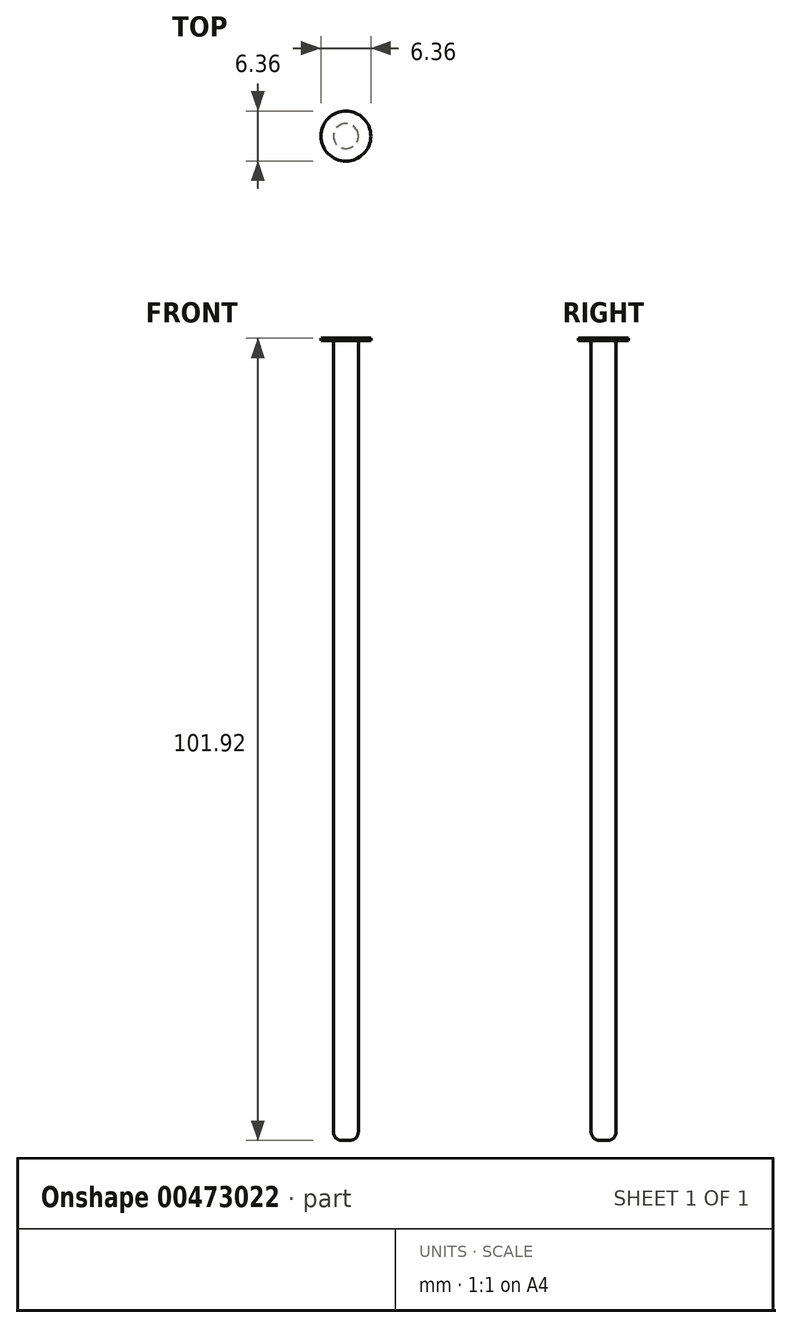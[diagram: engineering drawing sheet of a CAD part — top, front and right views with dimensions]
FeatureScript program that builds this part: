
annotation { "Feature Type Name" : "Feature", "Feature Type Description" : "" }
export const myFeature = defineFeature(function(context is Context, id is Id, definition is map)
    precondition{}
    {
        {
            var Q0;
            Q0=qCreatedBy(makeId("Top.planeOp"),FACE);
            var sketch = newSketch(context, id + "F0", { "sketchPlane" : qUnion([Q0])});
            skCircle(sketch, "E0", {"center": v(0, 0) * mm, "radius": 1.59 * mm});
            skSolve(sketch);
        }
        {
            var Q0;
            Q0=makeQuery(id+"F0.imprint","IMPRINT",FACE,{"disambiguationData":[TD([[makeQuery(id+"F0.imprint","IMPRINT",EDGE,{"derivedFrom":sQuery(id+"F0.wireOp",EDGE,"E0")}),1.0]])]});
            extrude(context, id + "F1", {"entities" : qUnion([Q0]), "depth" : 101.6 * mm});
        }
        {
            var Q0;
            Q0=makeQuery(id+"F1.opExtrude","CAP_FACE",FACE,{"disambiguationData":[OSD([sQuery(id+"F0.wireOp",EDGE,"E0")])],"isStart":false});
            var sketch = newSketch(context, id + "F2", { "sketchPlane" : qUnion([Q0])});
            skCircle(sketch, "E1", {"center": v(0, 0) * mm, "radius": 3.18 * mm});
            skSolve(sketch);
        }
        {
            var Q0;
            Q0=makeQuery(id+"F2.imprint","IMPRINT",FACE,{"disambiguationData":[TD([[makeQuery(id+"F2.imprint","IMPRINT",EDGE,{"derivedFrom":sQuery(id+"F2.wireOp",EDGE,"E1")}),1.0]])]});
            var Q1;
            Q1=makeQuery(id+"F2.imprint","IMPRINT",FACE,{"disambiguationData":[TD([[makeQuery(id+"F2.imprint","IMPRINT",EDGE,{"derivedFrom":makeQuery(id+"F1.opExtrude","CAP_EDGE",EDGE,{"disambiguationData":[OSD([sQuery(id+"F0.wireOp",EDGE,"E0")])],"isStart":false})}),1.0]])]});
            extrude(context, id + "F3", {"entities" : qUnion([Q0, Q1]), "operationType" : NewBodyOperationType.ADD, "depth" : 0.32 * mm});
        }
        {
            var Q0;
            Q0=makeQuery(id+"F1.opExtrude","CAP_EDGE",EDGE,{"disambiguationData":[OSD([sQuery(id+"F0.wireOp",EDGE,"E0")])],"isStart":true});
            fillet(context, id + "F4", {"entities" : qUnion([Q0]), "radius" : 1.27 * mm, "tangentPropagation" : true, "rho" : 0.5, "crossSection" : FilletCrossSection.CONIC, "allowEdgeOverflow" : false});
        }
    });
